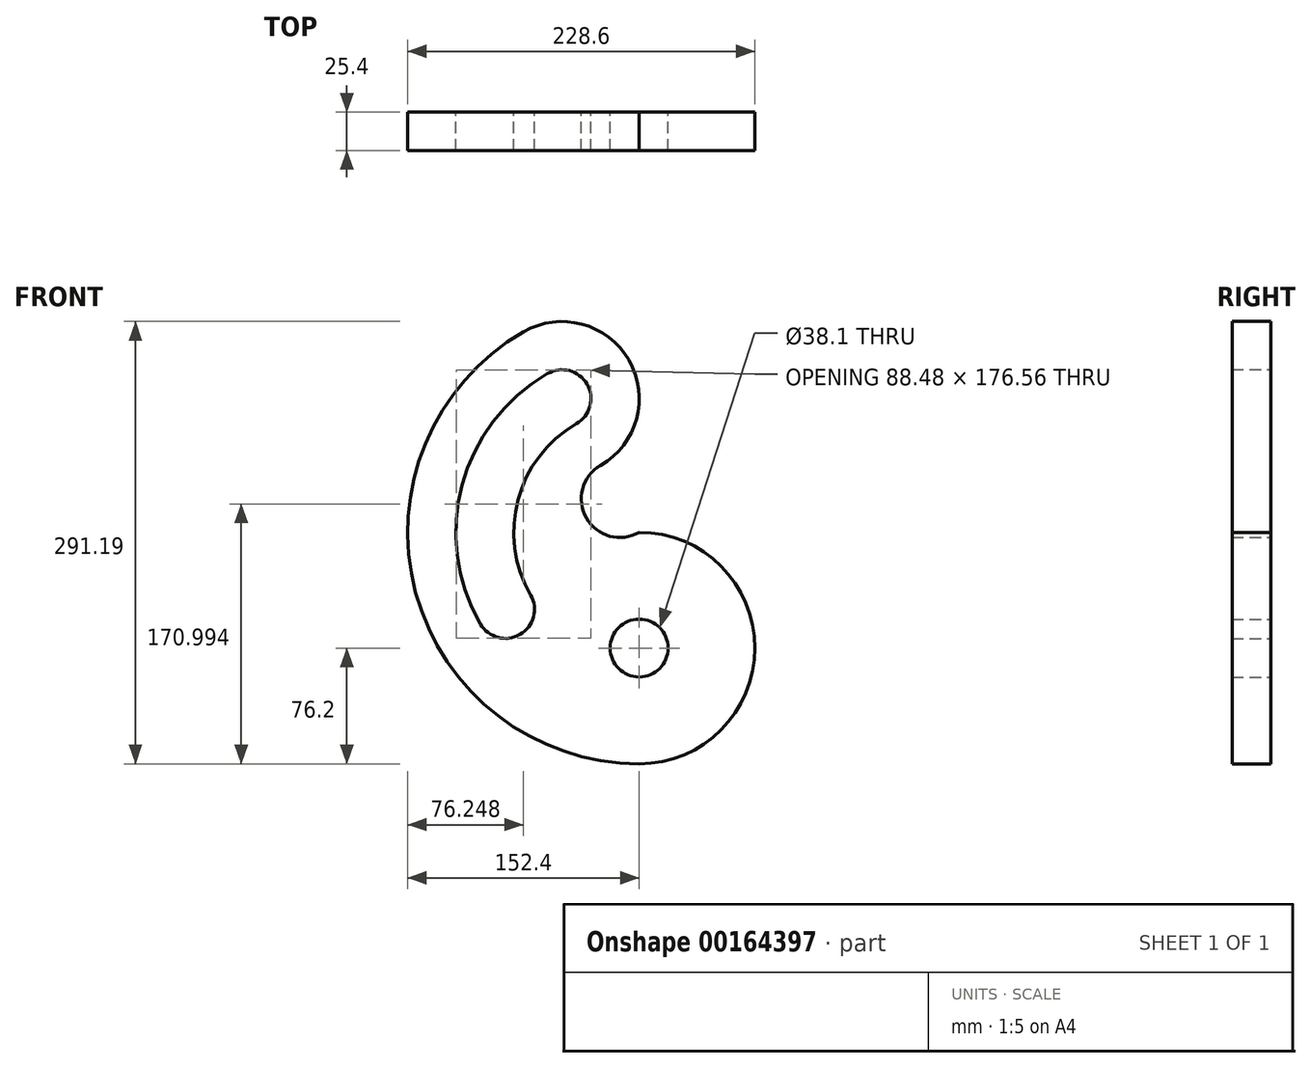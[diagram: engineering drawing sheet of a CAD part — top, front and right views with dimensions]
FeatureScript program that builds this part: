
annotation { "Feature Type Name" : "Feature", "Feature Type Description" : "" }
export const myFeature = defineFeature(function(context is Context, id is Id, definition is map)
    precondition{}
    {
        {
            var Q0;
            Q0=qCreatedBy(makeId("Front.planeOp"),FACE);
            var sketch = newSketch(context, id + "F0", { "sketchPlane" : qUnion([Q0])});
            skCircle(sketch, "E0", {"center": v(0, 0) * mm, "radius": 19.05 * mm});
            skLineSegment(sketch, "E1", {"start": v(0, 76.2) * mm, "end": v(0, -76.2) * mm, "construction": true});
            skLineSegment(sketch, "E2", {"start": v(0, 76.2) * mm, "end": v(-263.96, -76.2) * mm, "construction": true});
            skLineSegment(sketch, "E3", {"start": v(0, 76.2) * mm, "end": v(0, 76.2) * mm});
            skLineSegment(sketch, "E4", {"start": v(76.2, 0) * mm, "end": v(120.47, 0) * mm, "construction": true});
            skArc(sketch, "E5", {"start": v(0, -76.2) * mm, "mid": v(76.2, 0) * mm, "end": v(0, 76.2) * mm});
            skLineSegment(sketch, "E6", {"start": v(0, 76.2) * mm, "end": v(-263.96, 533.4) * mm, "construction": true});
            skLineSegment(sketch, "E7", {"start": v(0, 76.2) * mm, "end": v(0, 124.82) * mm, "construction": true});
            skArc(sketch, "E8", {"start": v(-25.4, 120.2) * mm, "mid": v(-34.7, 85.5) * mm, "end": v(0, 76.2) * mm});
            skArc(sketch, "E9", {"start": v(-25.4, 120.2) * mm, "mid": v(-6.8, 189.59) * mm, "end": v(-76.2, 208.18) * mm});
            skArc(sketch, "E10", {"start": v(-76.2, 208.18) * mm, "mid": v(-147.2, 36.76) * mm, "end": v(0, -76.2) * mm});
            skArc(sketch, "E11", {"start": v(-50.8, 164.19) * mm, "mid": v(-98.14, 102.5) * mm, "end": v(-87.99, 25.4) * mm, "construction": true});
            skCircle(sketch, "E12", {"center": v(-50.8, 164.19) * mm, "radius": 19.05 * mm});
            skCircle(sketch, "E13", {"center": v(-87.99, 25.4) * mm, "radius": 19.05 * mm});
            skArc(sketch, "E14", {"start": v(-60.33, 180.69) * mm, "mid": v(-116.54, 107.43) * mm, "end": v(-104.49, 15.87) * mm});
            skArc(sketch, "E15", {"start": v(-41.27, 147.7) * mm, "mid": v(-79.74, 97.57) * mm, "end": v(-71.5, 34.92) * mm});
            skPoint(sketch, "E16", {"position": v(-50.07, 164.6) * mm});
            skSolve(sketch);
        }
        {
            var Q0;
            Q0=makeQuery(id+"F0.imprint","IMPRINT",FACE,{"disambiguationData":[TD([[makeQuery(id+"F0.imprint","IMPRINT",EDGE,{"derivedFrom":sQuery(id+"F0.wireOp",EDGE,"E0")}),-1.0]])]});
            extrude(context, id + "F1", {"entities" : qUnion([Q0]), "depth" : 25.4 * mm});
        }
    });
